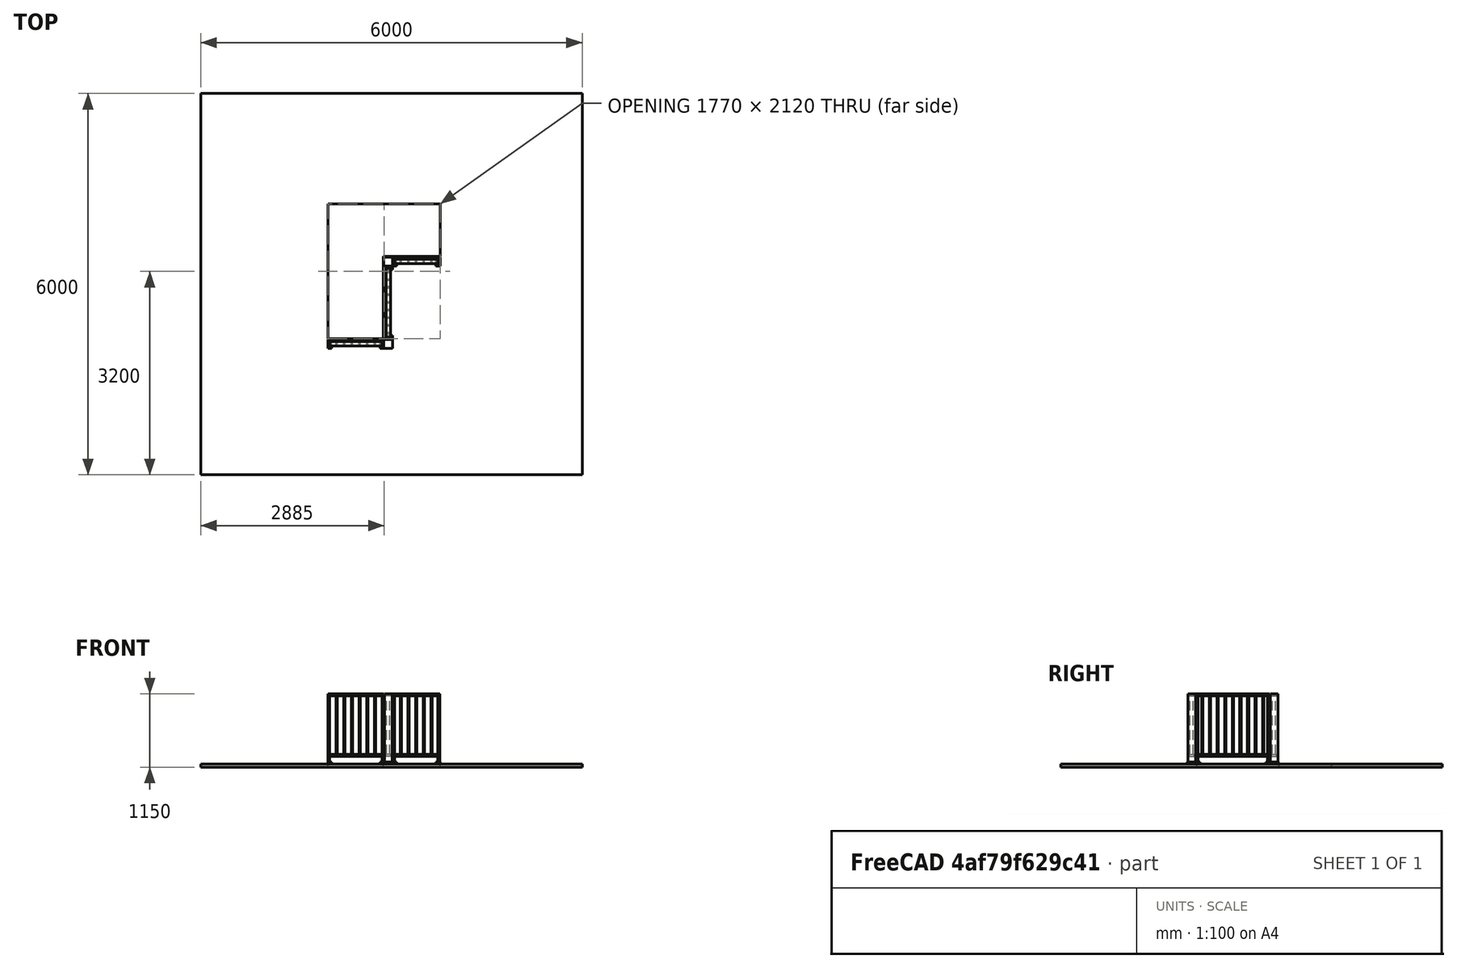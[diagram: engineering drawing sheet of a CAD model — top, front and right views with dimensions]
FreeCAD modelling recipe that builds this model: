
FCSTD DOCUMENT  (FreeCAD 0.18R16146 (Git))
Label: guarda-corpo-assembly
License: All rights reserved
LicenseURL: http://en.wikipedia.org/wiki/All_rights_reserved
objects: TechDraw::DrawViewDimension×12, Part::Box×9, Part::Cut×3, Part::Feature×3, TechDraw::DrawSVGTemplate×3, TechDraw::DrawViewPart×3, TechDraw::DrawPage×3, Spreadsheet::Sheet×1, Part::Fuse×1
note: 16 computed .brp shape members not serialized (recipe doc carries the construction recipe); baked Part::Feature solids carry a one-line shape summary decoded from their .brp

FEATURE [Spreadsheet::Sheet] Spreadsheet  label="assembly"
  cells = B1=altura (height); C1=frente (length); D1=profundidade (width); E1=z; F1=x; G1=y; H1=quantidade; A2=modulo_1; E2(modulo_1_z)=30; F2(modulo_1_x)=0; G2(modulo_1_y)=0; H2=1; A3=modulo_2; E3(modulo_2_z)=30; F3(modulo_2_x)=1010; G3(modulo_2_y)=130; H3=1; A4=modulo_3; E4(modulo_3_z)=30; F4(modulo_3_x)=1020; G4(modulo_3_y)=1295; H4=1; A5=base_1; B5(base_1_height)=30; C5(base_1_length)=60; D5(base_1_width)=140; E5(base_1_z)=0; F5(base_1_x)=0; G5(base_1_y)=-10; A6=base_2_fora; B6(base_2_fora_height)=30; C6(base_2_fora_length)=200; D6(base_2_fora_width)=200; E6(base_2_fora_z)=0; F6(base_2_fora_x)=820; G6(base_2_fora_y)=-10; A7=base_2_recorte; B7(base_2_recorte_height)=30; C7(base_2_recorte_length)=60; D7(base_2_recorte_width)=60; E7(base_2_recorte_z)=0; F7(base_2_recorte_x)=820; G7(base_2_recorte_y)=130; A8=base_3_fora; B8(base_3_fora_height)=30; C8(base_3_fora_length)=200; D8(base_3_fora_width)=200; E8(base_3_fora_z)=0; F8(base_3_fora_x)=880; G8(base_3_fora_y)=1225; A9=base_3_recorte; B9(base_3_recorte_height)=30; C9(base_3_recorte_length)=60; D9(base_3_recorte_width)=60; E9(base_3_recorte_z)=0; F9(base_3_recorte_x)=1020; G9(base_3_recorte_y)=1225; A10=base_4; B10(base_4_height)=30; C10(base_4_length)=70; D10(base_4_width)=140; E10(base_4_z)=0; F10(base_4_x)=1700; G10(base_4_y)=1285
FEATURE [Part::Box] Box  label="vao1"
  AttacherType = Attacher::AttachEngine3D
  Height = 50
  Length = 870
  Placement = pos=(0,0,-50) rot=(0,0,1;0rad)
  Width = 2120
  expr: Placement.Base.z = -vao1.Height
FEATURE [Part::Box] Box001  label="vao2"
  AttacherType = Attacher::AttachEngine3D
  Height = 50
  Length = 900
  Placement = pos=(870,1295,-50) rot=(0,0,1;0rad)
  Width = 825
  expr: Placement.Base.x = vao1.Length
  expr: Placement.Base.z = -vao2.Height
FEATURE [Part::Fuse] Fusion  label="vao"
  Base = -> Box
  Placement = pos=(0,140,0) rot=(0,0,1;0rad)
  Tool = -> Box001
FEATURE [Part::Box] Box002  label="laje"
  AttacherType = Attacher::AttachEngine3D
  Height = 50
  Length = 6000
  Placement = pos=(-2000,-2000,-50) rot=(0,0,1;0rad)
  Width = 6000
  expr: Placement.Base.z = -laje.Height
FEATURE [Part::Cut] Cut  label="vao_na_laje"
  Base = -> Box002
  Tool = -> Fusion
FEATURE [Part::Box] Box003  label="base_1"
  AttacherType = Attacher::AttachEngine3D
  Height = 30
  Length = 60
  Placement = pos=(0,-10,0) rot=(0,0,1;0rad)
  Width = 140
  expr: Width = assembly.base_1_width
  expr: Length = assembly.base_1_length
  expr: Placement.Base.z = assembly.base_1_z
  expr: Placement.Base.y = assembly.base_1_y
  expr: Height = assembly.base_1_height
  expr: Placement.Base.x = assembly.base_1_x
FEATURE [Part::Box] Box004  label="base_2_fora"
  AttacherType = Attacher::AttachEngine3D
  Height = 30
  Length = 200
  Placement = pos=(820,-10,0) rot=(0,0,1;0rad)
  Width = 200
  expr: Width = assembly.base_2_fora_width
  expr: Length = assembly.base_2_fora_length
  expr: Placement.Base.z = assembly.base_2_fora_z
  expr: Placement.Base.y = assembly.base_2_fora_y
  expr: Height = assembly.base_2_fora_height
  expr: Placement.Base.x = assembly.base_2_fora_x
FEATURE [Part::Box] Box005  label="base_2_recorte"
  AttacherType = Attacher::AttachEngine3D
  Height = 30
  Length = 60
  Placement = pos=(820,130,0) rot=(0,0,1;0rad)
  Width = 60
  expr: Width = assembly.base_2_recorte_width
  expr: Length = assembly.base_2_recorte_length
  expr: Placement.Base.z = assembly.base_2_recorte_z
  expr: Placement.Base.y = assembly.base_2_recorte_y
  expr: Height = assembly.base_2_recorte_height
  expr: Placement.Base.x = assembly.base_2_recorte_x
FEATURE [Part::Cut] Cut001  label="base_2"
  Base = -> Box004
  Tool = -> Box005
FEATURE [Part::Box] Box006  label="base_3_fora"
  AttacherType = Attacher::AttachEngine3D
  Height = 30
  Length = 200
  Placement = pos=(880,1225,0) rot=(0,0,1;0rad)
  Width = 200
  expr: Width = assembly.base_3_fora_width
  expr: Length = assembly.base_3_fora_length
  expr: Placement.Base.z = assembly.base_3_fora_z
  expr: Placement.Base.y = assembly.base_3_fora_y
  expr: Height = assembly.base_3_fora_height
  expr: Placement.Base.x = assembly.base_3_fora_x
FEATURE [Part::Box] Box007  label="base_3_recorte"
  AttacherType = Attacher::AttachEngine3D
  Height = 30
  Length = 60
  Placement = pos=(1020,1225,0) rot=(0,0,1;0rad)
  Width = 60
  expr: Width = assembly.base_3_recorte_width
  expr: Length = assembly.base_3_recorte_length
  expr: Placement.Base.z = assembly.base_3_recorte_z
  expr: Placement.Base.y = assembly.base_3_recorte_y
  expr: Height = assembly.base_3_recorte_height
  expr: Placement.Base.x = assembly.base_3_recorte_x
FEATURE [Part::Cut] Cut002  label="base_3"
  Base = -> Box006
  Tool = -> Box007
FEATURE [Part::Box] Box008  label="base_4"
  AttacherType = Attacher::AttachEngine3D
  Height = 30
  Length = 70
  Placement = pos=(1700,1285,0) rot=(0,0,1;0rad)
  Width = 140
  expr: Width = assembly.base_4_width
  expr: Length = assembly.base_4_length
  expr: Placement.Base.z = assembly.base_4_z
  expr: Placement.Base.y = assembly.base_4_y
  expr: Height = assembly.base_4_height
  expr: Placement.Base.x = assembly.base_4_x
FEATURE [Part::Feature] Compound001  label="modulo_1_copy"
  Placement = pos=(0,0,30) rot=(0,0,1;0rad)
  shape: bbox 880 x 120 x 1070 mm, 60 faces, 10 solids (baked)
  expr: Placement.Base.z = assembly.modulo_1_z
  expr: Placement.Base.y = assembly.modulo_1_y
  expr: Placement.Base.x = assembly.modulo_1_x
FEATURE [Part::Feature] Compound002  label="modulo_2_copy"
  Placement = pos=(1010,130,30) rot=(0,0,1;1.5708rad)
  shape: bbox 120 x 1155 x 1070 mm, 78 faces, 13 solids (baked)
  expr: Placement.Base.z = assembly.modulo_2_z
  expr: Placement.Base.y = assembly.modulo_2_y
  expr: Placement.Base.x = assembly.modulo_2_x
FEATURE [Part::Feature] Compound003  label="modulo_3_copy"
  Placement = pos=(1020,1295,30) rot=(0,0,1;0rad)
  shape: bbox 740 x 120 x 1070 mm, 54 faces, 9 solids (baked)
  expr: Placement.Base.z = assembly.modulo_3_z
  expr: Placement.Base.y = assembly.modulo_3_y
  expr: Placement.Base.x = assembly.modulo_3_x
FEATURE [TechDraw::DrawSVGTemplate] Template
  Height = 420
  Orientation = 1
  Width = 594
FEATURE [TechDraw::DrawViewPart] View
  CoarseView = false
  Direction = (0.577,-0.577,0.577)
  Focus = 100
  HardHidden = false
  IsoCount = 0
  IsoHidden = false
  IsoVisible = false
  LockPosition = false
  Perspective = false
  Rotation = 0
  Scale = 0.2
  ScaleType = 0
  SeamHidden = false
  SeamVisible = false
  SmoothHidden = false
  SmoothVisible = false
  Source = -> [Box003,Cut001,Cut002,Box008,Compound001,Compound002,Compound003]
  X = 297
  Y = 210
FEATURE [TechDraw::DrawPage] Page  label="Isometrica"
  KeepUpdated = true
  ProjectionType = 0
  Template = -> Template
  Views = -> [View]
FEATURE [TechDraw::DrawSVGTemplate] Template001
  Height = 420
  Orientation = 1
  Width = 594
FEATURE [TechDraw::DrawViewPart] View001
  CoarseView = false
  Direction = (0,0,1)
  Focus = 100
  HardHidden = false
  IsoCount = 0
  IsoHidden = false
  IsoVisible = false
  LockPosition = false
  Perspective = false
  Rotation = 0
  Scale = 0.2
  ScaleType = 0
  SeamHidden = false
  SeamVisible = false
  SmoothHidden = false
  SmoothVisible = false
  Source = -> [Box003,Cut001,Cut002,Box008,Compound001,Compound002,Compound003]
  X = 297
  Y = 210
FEATURE [TechDraw::DrawViewDimension] Dimension
  Arbitrary = false
  FormatSpec = %.0f
  LockPosition = false
  MeasureType = 1
  OverTolerance = 0
  References2D = -> [View001]
  Rotation = 0
  ScaleType = 0
  Type = 1
  UnderTolerance = 0
  X = -87.6308
  Y = -96.4511
FEATURE [TechDraw::DrawViewDimension] Dimension001
  Arbitrary = false
  FormatSpec = %.0f
  LockPosition = false
  MeasureType = 1
  OverTolerance = 0
  References2D = -> [View001]
  Rotation = 0
  ScaleType = 0
  Type = 2
  UnderTolerance = 0
  X = 36.4303
  Y = -9.24205
FEATURE [TechDraw::DrawViewDimension] Dimension002
  Arbitrary = false
  FormatSpec = %.0f
  LockPosition = false
  MeasureType = 1
  OverTolerance = 0
  References2D = -> [View001]
  Rotation = 0
  ScaleType = 0
  Type = 1
  UnderTolerance = 0
  X = 100.315
  Y = 159.468
FEATURE [TechDraw::DrawViewDimension] Dimension003
  Arbitrary = false
  FormatSpec = %.0f
  LockPosition = false
  MeasureType = 1
  OverTolerance = 0
  References2D = -> [View001]
  Rotation = 0
  ScaleType = 0
  Type = 2
  UnderTolerance = 0
  X = -19.1418
  Y = 124.527
FEATURE [TechDraw::DrawViewDimension] Dimension004
  Arbitrary = false
  FormatSpec = %.0f
  LockPosition = false
  MeasureType = 1
  OverTolerance = 0
  References2D = -> [View001]
  Rotation = 0
  ScaleType = 0
  Type = 1
  UnderTolerance = 0
  X = 8.55674
  Y = -155.537
FEATURE [TechDraw::DrawViewDimension] Dimension005
  Arbitrary = false
  FormatSpec = %.0f
  LockPosition = false
  MeasureType = 1
  OverTolerance = 0
  References2D = -> [View001]
  Rotation = 0
  ScaleType = 0
  Type = 1
  UnderTolerance = 0
  X = -171
  Y = -154.94
FEATURE [TechDraw::DrawViewDimension] Dimension006
  Arbitrary = false
  FormatSpec = %.0f
  LockPosition = false
  MeasureType = 1
  OverTolerance = 0
  References2D = -> [View001]
  Rotation = 0
  ScaleType = 0
  Type = 1
  UnderTolerance = 0
  X = 170
  Y = 110.448
FEATURE [TechDraw::DrawViewDimension] Dimension007
  Arbitrary = false
  FormatSpec = %.0f
  LockPosition = false
  MeasureType = 1
  OverTolerance = 0
  References2D = -> [View001]
  Rotation = 0
  ScaleType = 0
  Type = 2
  UnderTolerance = 0
  X = 187.629
  Y = 127.395
FEATURE [TechDraw::DrawViewDimension] Dimension008
  Arbitrary = false
  FormatSpec = %.0f
  LockPosition = false
  MeasureType = 1
  OverTolerance = 0
  References2D = -> [View001]
  Rotation = 0
  ScaleType = 0
  Type = 2
  UnderTolerance = 0
  X = -194.714
  Y = -128.971
FEATURE [TechDraw::DrawPage] Page001  label="Topo"
  KeepUpdated = true
  ProjectionType = 0
  Template = -> Template001
  Views = -> [View001,Dimension,Dimension001,Dimension002,Dimension003,Dimension004,Dimension005,Dimension006,Dimension007,Dimension008]
FEATURE [TechDraw::DrawSVGTemplate] Template002
  Height = 420
  Orientation = 1
  Width = 594
FEATURE [TechDraw::DrawViewPart] View002
  CoarseView = false
  Direction = (-1,0,0)
  Focus = 100
  HardHidden = false
  IsoCount = 0
  IsoHidden = false
  IsoVisible = false
  LockPosition = false
  Perspective = false
  Rotation = 0
  Scale = 0.2
  ScaleType = 0
  SeamHidden = false
  SeamVisible = false
  SmoothHidden = false
  SmoothVisible = false
  Source = -> [Box003,Cut001,Cut002,Box008,Compound001,Compound002,Compound003]
  X = 257.186
  Y = 210
FEATURE [TechDraw::DrawViewDimension] Dimension009
  Arbitrary = false
  FormatSpec = %.0f
  LockPosition = false
  MeasureType = 1
  OverTolerance = 0
  References2D = -> [View002]
  Rotation = 0
  ScaleType = 0
  Type = 2
  UnderTolerance = 0
  X = -160.326
  Y = 2.6577
FEATURE [TechDraw::DrawViewDimension] Dimension010
  Arbitrary = false
  FormatSpec = %.0f
  LockPosition = false
  MeasureType = 1
  OverTolerance = 0
  References2D = -> [View002]
  Rotation = 0
  ScaleType = 0
  Type = 2
  UnderTolerance = 0
  X = -160.377
  Y = -105.578
FEATURE [TechDraw::DrawViewDimension] Dimension011
  Arbitrary = false
  FormatSpec = %.0f
  LockPosition = false
  MeasureType = 1
  OverTolerance = 0
  References2D = -> [View002]
  Rotation = 0
  ScaleType = 0
  Type = 2
  UnderTolerance = 0
  X = -92.1247
  Y = -95.8531
FEATURE [TechDraw::DrawPage] Page002  label="Frente"
  KeepUpdated = true
  ProjectionType = 0
  Template = -> Template002
  Views = -> [View002,Dimension009,Dimension010,Dimension011]
